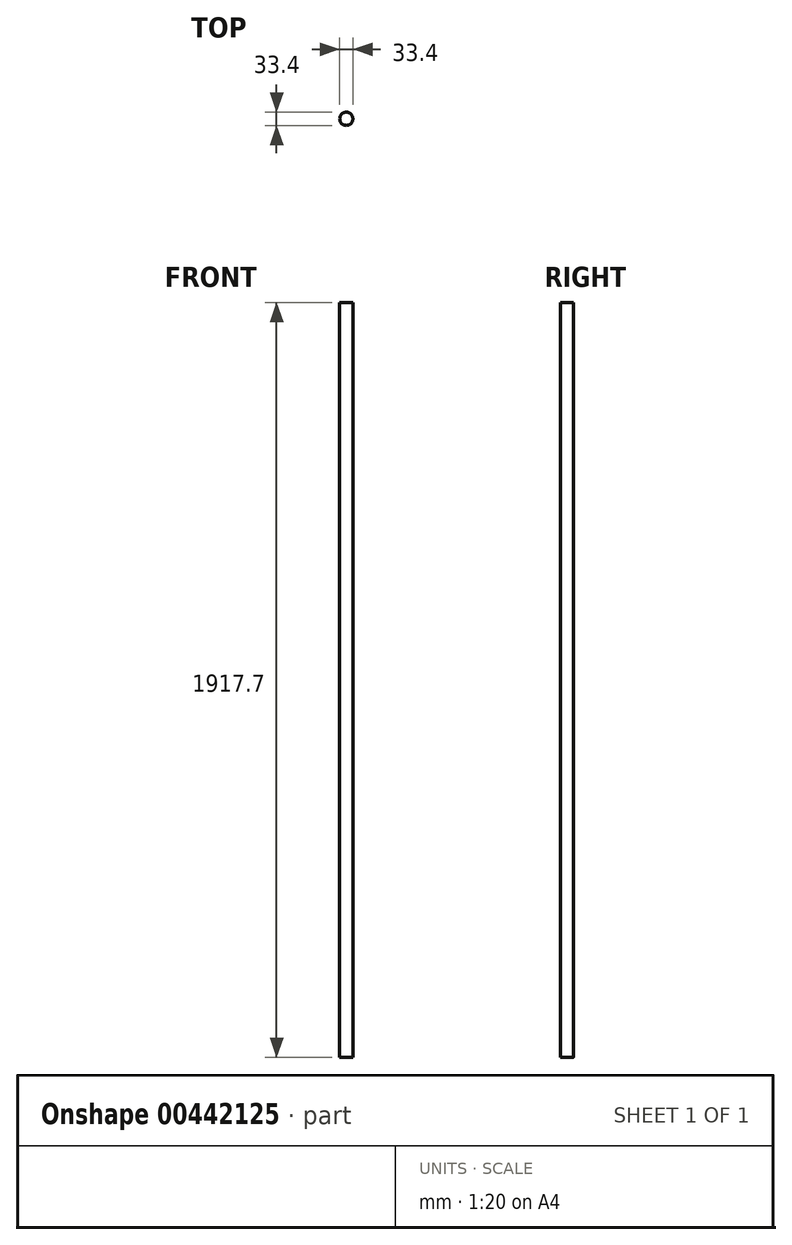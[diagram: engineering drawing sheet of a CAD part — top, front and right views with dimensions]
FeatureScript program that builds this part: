
annotation { "Feature Type Name" : "Feature", "Feature Type Description" : "" }
export const myFeature = defineFeature(function(context is Context, id is Id, definition is map)
    precondition{}
    {
        {
            var Q0;
            Q0=qCreatedBy(makeId("Top.planeOp"),FACE);
            var sketch = newSketch(context, id + "F0", { "sketchPlane" : qUnion([Q0])});
            skCircle(sketch, "E0", {"center": v(0, 0) * mm, "radius": 16.7 * mm});
            skSolve(sketch);
        }
        {
            var Q0;
            Q0=qSketchRegion(id+"F0",true);
            extrude(context, id + "F1", {"entities" : qUnion([Q0]), "depth" : 1917.7 * mm});
        }
    });
